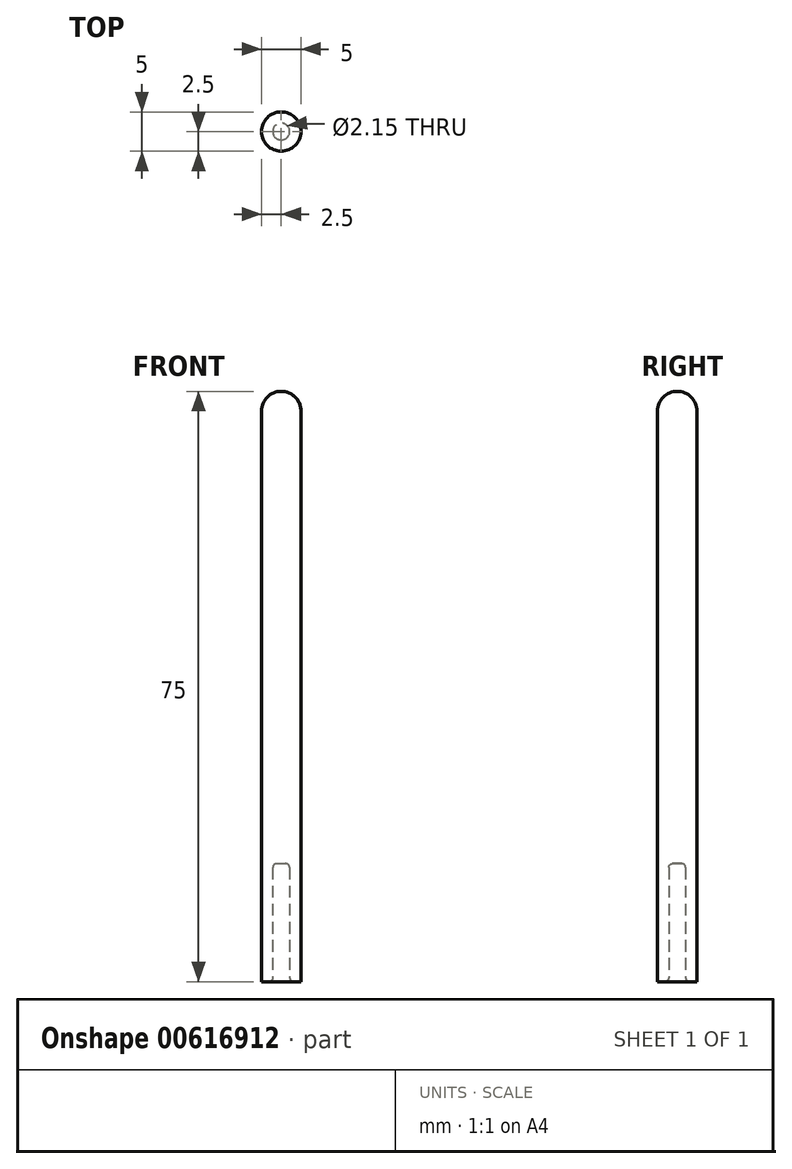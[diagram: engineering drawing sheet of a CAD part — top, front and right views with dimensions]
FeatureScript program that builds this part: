
annotation { "Feature Type Name" : "Feature", "Feature Type Description" : "" }
export const myFeature = defineFeature(function(context is Context, id is Id, definition is map)
    precondition{}
    {
        {
            var Q0;
            Q0=qCreatedBy(makeId("Top.planeOp"),FACE);
            var sketch = newSketch(context, id + "F0", { "sketchPlane" : qUnion([Q0])});
            skCircle(sketch, "E0", {"center": v(0, 0) * mm, "radius": 2.5 * mm});
            skSolve(sketch);
        }
        {
            var Q0;
            Q0=makeQuery(id+"F0.imprint","IMPRINT",FACE,{"disambiguationData":[TD([[makeQuery(id+"F0.imprint","IMPRINT",EDGE,{"derivedFrom":sQuery(id+"F0.wireOp",EDGE,"E0")}),1.0]])]});
            extrude(context, id + "F1", {"entities" : qUnion([Q0]), "depth" : 75 * mm, "offsetDistance" : 25 * mm});
        }
        {
            var Q0;
            Q0=makeQuery(id+"F1.opExtrude","CAP_FACE",FACE,{"disambiguationData":[OSD([sQuery(id+"F0.wireOp",EDGE,"E0")])],"isStart":false});
            fillet(context, id + "F2", {"entities" : qUnion([Q0]), "radius" : 2.5 * mm, "tangentPropagation" : true, "allowEdgeOverflow" : false});
        }
        {
            var Q0;
            Q0=makeQuery(id+"F1.opExtrude","CAP_FACE",FACE,{"disambiguationData":[OSD([sQuery(id+"F0.wireOp",EDGE,"E0")])],"isStart":true});
            var sketch = newSketch(context, id + "F3", { "sketchPlane" : qUnion([Q0])});
            skCircle(sketch, "E1", {"center": v(0, 0) * mm, "radius": 1.07 * mm});
            skSolve(sketch);
        }
        {
            var Q0;
            Q0=makeQuery(id+"F3.imprint","IMPRINT",FACE,{"disambiguationData":[TD([[makeQuery(id+"F3.imprint","IMPRINT",EDGE,{"derivedFrom":sQuery(id+"F3.wireOp",EDGE,"E1")}),1.0]])]});
            extrude(context, id + "F4", {"entities" : qUnion([Q0]), "operationType" : NewBodyOperationType.REMOVE, "oppositeDirection" : true, "depth" : 15 * mm, "offsetDistance" : 25 * mm});
        }
        {
            var Q0;
            Q0=makeQuery(id+"F4.boolean.opBoolean","COPY",EDGE,{"derivedFrom":makeQuery(id+"F4.opExtrude","CAP_EDGE",EDGE,{"disambiguationData":[OSD([sQuery(id+"F3.wireOp",EDGE,"E1")])],"isStart":true})});
            var Q1;
            Q1=makeQuery(id+"F4.boolean.opBoolean","COPY",FACE,{"derivedFrom":makeQuery(id+"F4.opExtrude","SWEPT_FACE",FACE,{"disambiguationData":[OSD([sQuery(id+"F3.wireOp",EDGE,"E1")])]})});
            fillet(context, id + "F5", {"entities" : qUnion([Q0, Q1]), "radius" : .5 * mm, "tangentPropagation" : true, "allowEdgeOverflow" : false});
        }
    });
